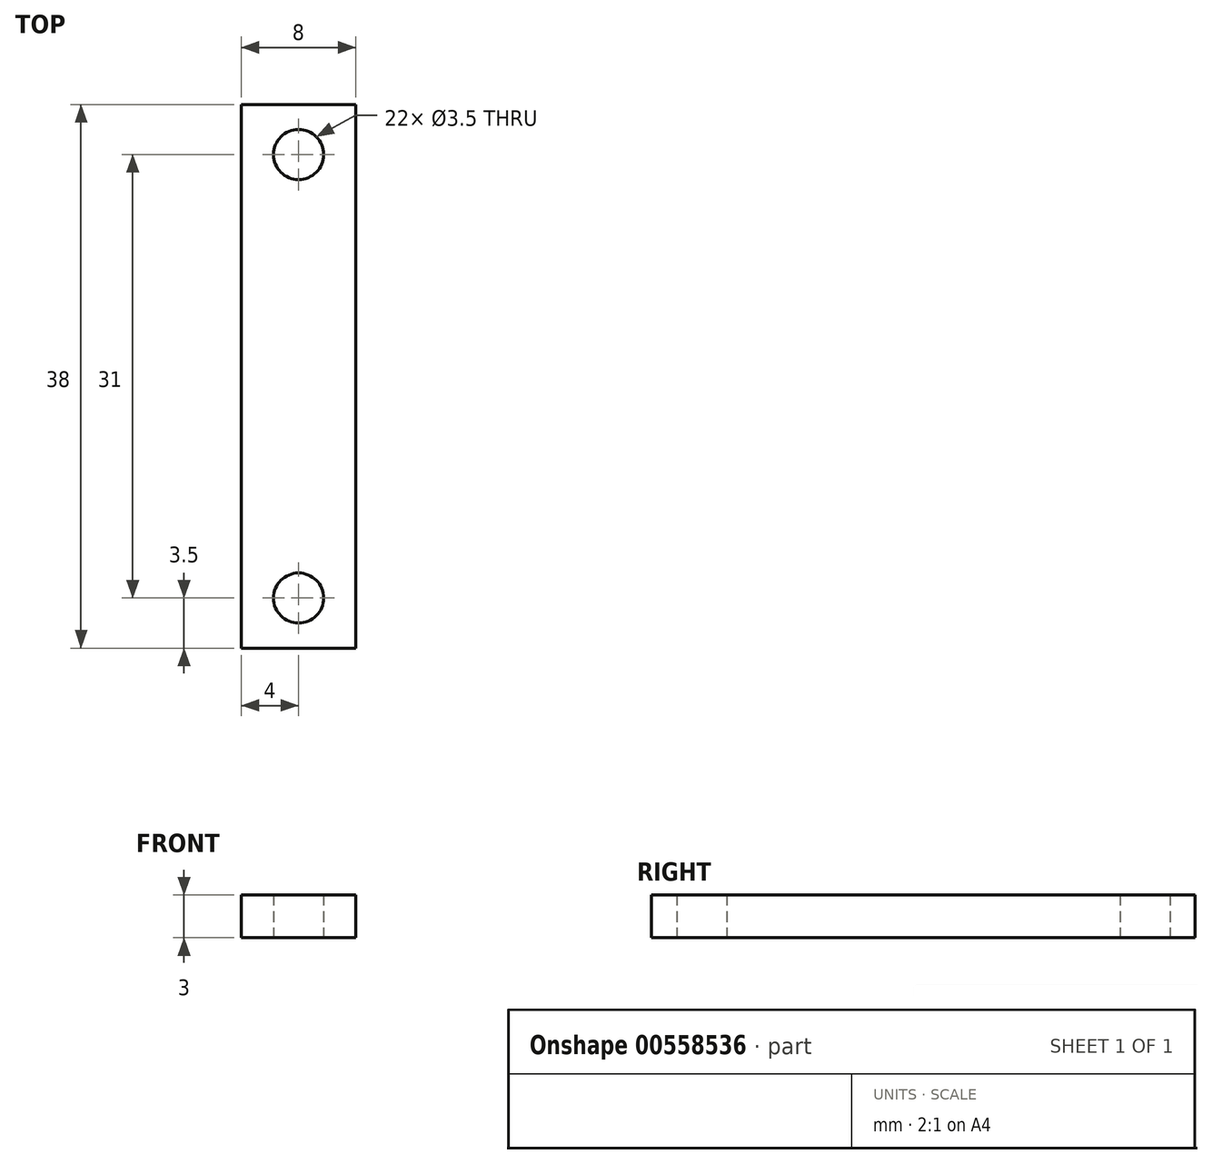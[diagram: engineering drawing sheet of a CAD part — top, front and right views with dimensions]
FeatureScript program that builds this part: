
annotation { "Feature Type Name" : "Feature", "Feature Type Description" : "" }
export const myFeature = defineFeature(function(context is Context, id is Id, definition is map)
    precondition{}
    {
        {
            var Q0;
            Q0=qCreatedBy(makeId("Top.planeOp"),FACE);
            var sketch = newSketch(context, id + "F0", { "sketchPlane" : qUnion([Q0])});
            skLineSegment(sketch, "E0.bottom", {"start": v(-4, 19) * mm, "end": v(4, 19) * mm});
            skLineSegment(sketch, "E0.top", {"start": v(-4, -19) * mm, "end": v(4, -19) * mm});
            skLineSegment(sketch, "E0.left", {"start": v(-4, 19) * mm, "end": v(-4, -19) * mm});
            skLineSegment(sketch, "E0.right", {"start": v(4, 19) * mm, "end": v(4, -19) * mm});
            skPoint(sketch, "E0.middle", {"position": v(0, 0) * mm});
            skCircle(sketch, "E1", {"center": v(0, 15.5) * mm, "radius": 1.75 * mm});
            skCircle(sketch, "E2.MirrorC", {"center": v(0, -15.5) * mm, "radius": 1.75 * mm});
            skSolve(sketch);
        }
        {
            var Q0;
            Q0=makeQuery(id+"F0.imprint","IMPRINT",FACE,{"disambiguationData":[TD([[makeQuery(id+"F0.imprint","IMPRINT",EDGE,{"derivedFrom":sQuery(id+"F0.wireOp",EDGE,"E0.bottom")}),-1.0]])]});
            extrude(context, id + "F1", {"entities" : qUnion([Q0]), "depth" : 3 * mm, "offsetDistance" : 25 * mm});
        }
    });
